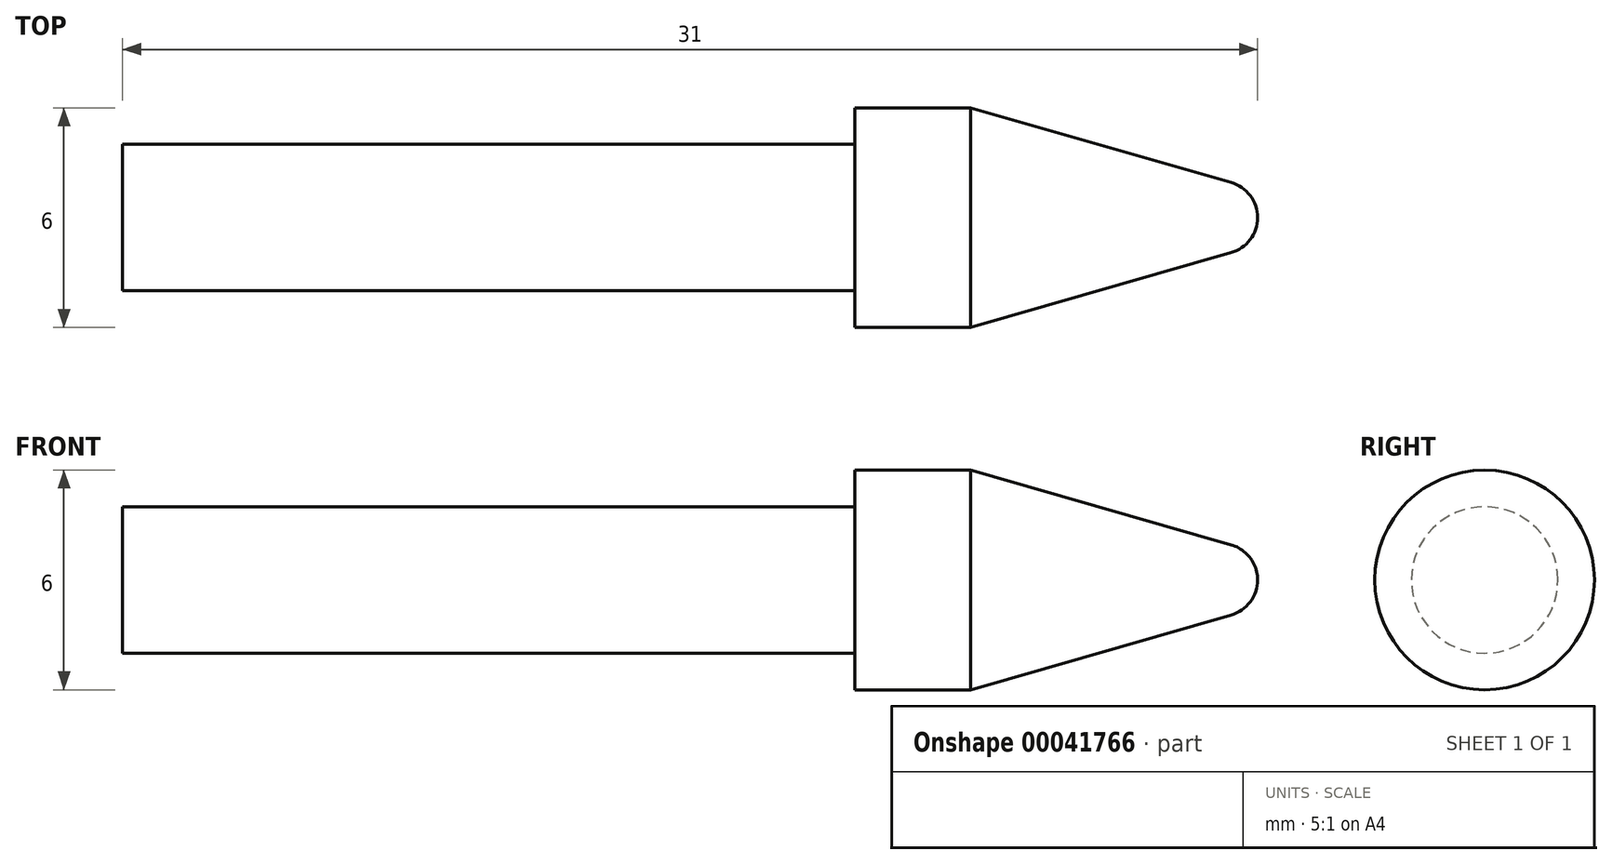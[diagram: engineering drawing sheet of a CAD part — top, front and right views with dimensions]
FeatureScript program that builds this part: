
annotation { "Feature Type Name" : "Feature", "Feature Type Description" : "" }
export const myFeature = defineFeature(function(context is Context, id is Id, definition is map)
    precondition{}
    {
        {
            var Q0;
            Q0=qCreatedBy(makeId("Front.planeOp"),FACE);
            var sketch = newSketch(context, id + "F0", { "sketchPlane" : qUnion([Q0])});
            skLineSegment(sketch, "E0", {"start": v(0, 0) * mm, "end": v(30, 0) * mm});
            skArc(sketch, "E1", {"start": v(31, 0) * mm, "mid": v(30.8, 0.6) * mm, "end": v(30.28, 0.96) * mm});
            skLineSegment(sketch, "E2", {"start": v(0, 0) * mm, "end": v(0, 2) * mm});
            skLineSegment(sketch, "E3", {"start": v(0, 2) * mm, "end": v(20, 2) * mm});
            skLineSegment(sketch, "E4", {"start": v(20, 2) * mm, "end": v(20, 3) * mm});
            skLineSegment(sketch, "E5", {"start": v(20, 3) * mm, "end": v(23.16, 3) * mm});
            skLineSegment(sketch, "E6", {"start": v(23.16, 3) * mm, "end": v(30.28, 0.96) * mm});
            skLineSegment(sketch, "E7", {"start": v(30, 0) * mm, "end": v(31, 0) * mm});
            skSolve(sketch);
        }
        {
            var Q0;
            Q0 = qSketchRegion(id + "F0", true);
            var Q1;
            Q1=sQuery(id+"F0.wireOp",EDGE,"E0");
            revolve(context, id + "F1", {"entities" : qUnion([Q0]), "axis" : qUnion([Q1]), "revolveType" : RevolveType.FULL});
        }
    });
